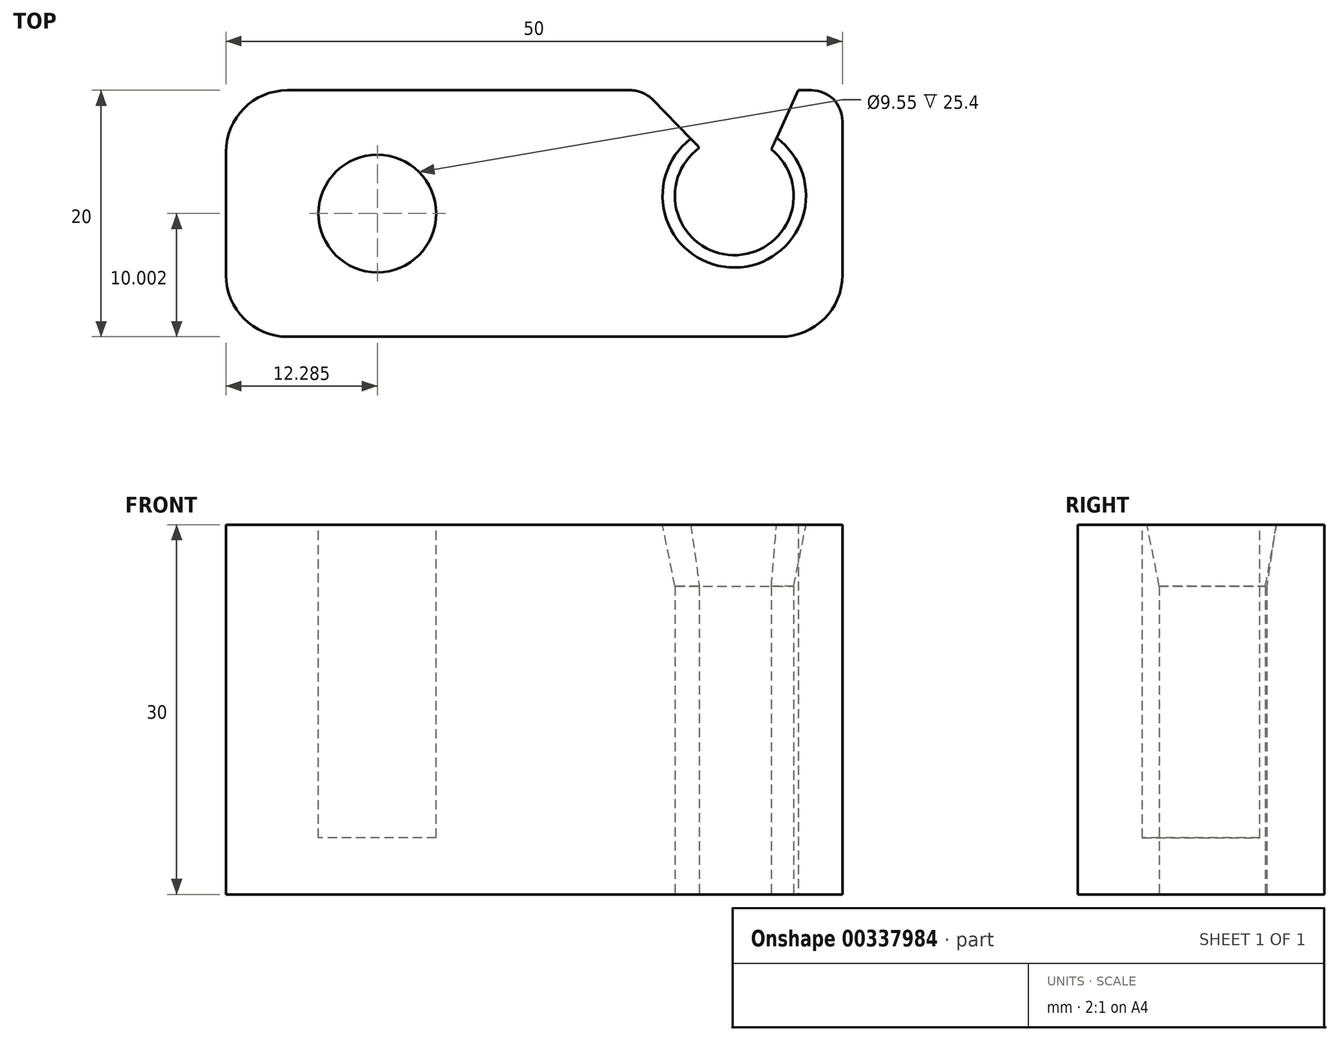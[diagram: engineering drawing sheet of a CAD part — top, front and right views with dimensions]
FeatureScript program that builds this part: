
annotation { "Feature Type Name" : "Feature", "Feature Type Description" : "" }
export const myFeature = defineFeature(function(context is Context, id is Id, definition is map)
    precondition{}
    {
        {
            var Q0;
            Q0=qCreatedBy(makeId("Top.planeOp"),FACE);
            var sketch = newSketch(context, id + "F0", { "sketchPlane" : qUnion([Q0])});
            skLineSegment(sketch, "E0.bottom", {"start": v(-25.26, -25.12) * mm, "end": v(8.6, -25.12) * mm});
            skLineSegment(sketch, "E0.top", {"start": v(-25.26, -45.12) * mm, "end": v(24.74, -45.12) * mm});
            skLineSegment(sketch, "E0.left", {"start": v(-25.26, -25.12) * mm, "end": v(-25.26, -45.12) * mm});
            skLineSegment(sketch, "E0.right", {"start": v(24.74, -25.12) * mm, "end": v(24.74, -45.12) * mm});
            skArc(sketch, "E1", {"start": v(13.14, -29.78) * mm, "mid": v(15.87, -38.5) * mm, "end": v(18.98, -29.9) * mm});
            skLineSegment(sketch, "E2", {"start": v(13.14, -29.78) * mm, "end": v(8.6, -25.12) * mm});
            skLineSegment(sketch, "E3", {"start": v(18.98, -29.9) * mm, "end": v(21.17, -25.12) * mm});
            skLineSegment(sketch, "E4.trimOffspring", {"start": v(21.17, -25.12) * mm, "end": v(24.74, -25.12) * mm});
            skSolve(sketch);
        }
        {
            var Q0;
            Q0 = qSketchRegion(id + "F0", true);
            extrude(context, id + "F1", {"entities" : qUnion([Q0]), "depth" : 30 * mm});
        }
        {
            var Q0;
            Q0=makeQuery(id+"F1.opExtrude","SWEPT_EDGE",EDGE,{"disambiguationData":[OSD([sQuery(id+"F0.wireOp",EDGE,"E0.bottom"),sQuery(id+"F0.wireOp",EDGE,"E0.left")])]});
            var Q1;
            Q1=makeQuery(id+"F1.opExtrude","SWEPT_EDGE",EDGE,{"disambiguationData":[OSD([sQuery(id+"F0.wireOp",EDGE,"E0.top"),sQuery(id+"F0.wireOp",EDGE,"E0.left")])]});
            var Q2;
            Q2=makeQuery(id+"F1.opExtrude","SWEPT_EDGE",EDGE,{"disambiguationData":[OSD([sQuery(id+"F0.wireOp",EDGE,"E0.top"),sQuery(id+"F0.wireOp",EDGE,"E0.right")])]});
            fillet(context, id + "F2", {"entities" : qUnion([Q0, Q1, Q2]), "radius" : 5 * mm, "tangentPropagation" : true, "allowEdgeOverflow" : false});
        }
        {
            var Q0;
            Q0=makeQuery(id+"F1.opExtrude","SWEPT_EDGE",EDGE,{"disambiguationData":[OSD([sQuery(id+"F0.wireOp",EDGE,"E0.right"),sQuery(id+"F0.wireOp",EDGE,"E4.trimOffspring")])]});
            var Q1;
            Q1=makeQuery(id+"F1.opExtrude","SWEPT_EDGE",EDGE,{"disambiguationData":[OSD([sQuery(id+"F0.wireOp",EDGE,"E0.bottom"),sQuery(id+"F0.wireOp",EDGE,"E2")])]});
            fillet(context, id + "F3", {"entities" : qUnion([Q0, Q1]), "radius" : 2.5 * mm, "tangentPropagation" : true, "allowEdgeOverflow" : false});
        }
        {
            var Q0;
            Q0=makeQuery(id+"F1.opExtrude","CAP_EDGE",EDGE,{"disambiguationData":[OSD([sQuery(id+"F0.wireOp",EDGE,"E1")])],"isStart":false});
            chamfer(context, id + "F4", {"entities" : qUnion([Q0]), "chamferType" : ChamferType.TWO_OFFSETS, "width1" : 5 * mm, "oppositeDirection" : false, "width2" : 1 * mm, "tangentPropagation" : true});
        }
        {
            var Q0;
            Q0=makeQuery(id+"F1.opExtrude","CAP_FACE",FACE,{"disambiguationData":[OSD([sQuery(id+"F0.wireOp",EDGE,"E0.bottom"),sQuery(id+"F0.wireOp",EDGE,"E0.top"),sQuery(id+"F0.wireOp",EDGE,"E0.left"),sQuery(id+"F0.wireOp",EDGE,"E0.right"),sQuery(id+"F0.wireOp",EDGE,"E1"),sQuery(id+"F0.wireOp",EDGE,"E2"),sQuery(id+"F0.wireOp",EDGE,"E3"),sQuery(id+"F0.wireOp",EDGE,"E4.trimOffspring")])],"isStart":false});
            var sketch = newSketch(context, id + "F5", { "sketchPlane" : qUnion([Q0])});
            skCircle(sketch, "E5", {"center": v(-12.97, -35.12) * mm, "radius": 4.77 * mm});
            skPoint(sketch, "E5.centerSnap0", {"position": v(-25.26, -35.12) * mm});
            skSolve(sketch);
        }
        {
            var Q0;
            Q0 = qSketchRegion(id + "F5", true);
            extrude(context, id + "F6", {"entities" : qUnion([Q0]), "operationType" : NewBodyOperationType.REMOVE, "oppositeDirection" : true, "depth" : 25.4 * mm});
        }
    });
